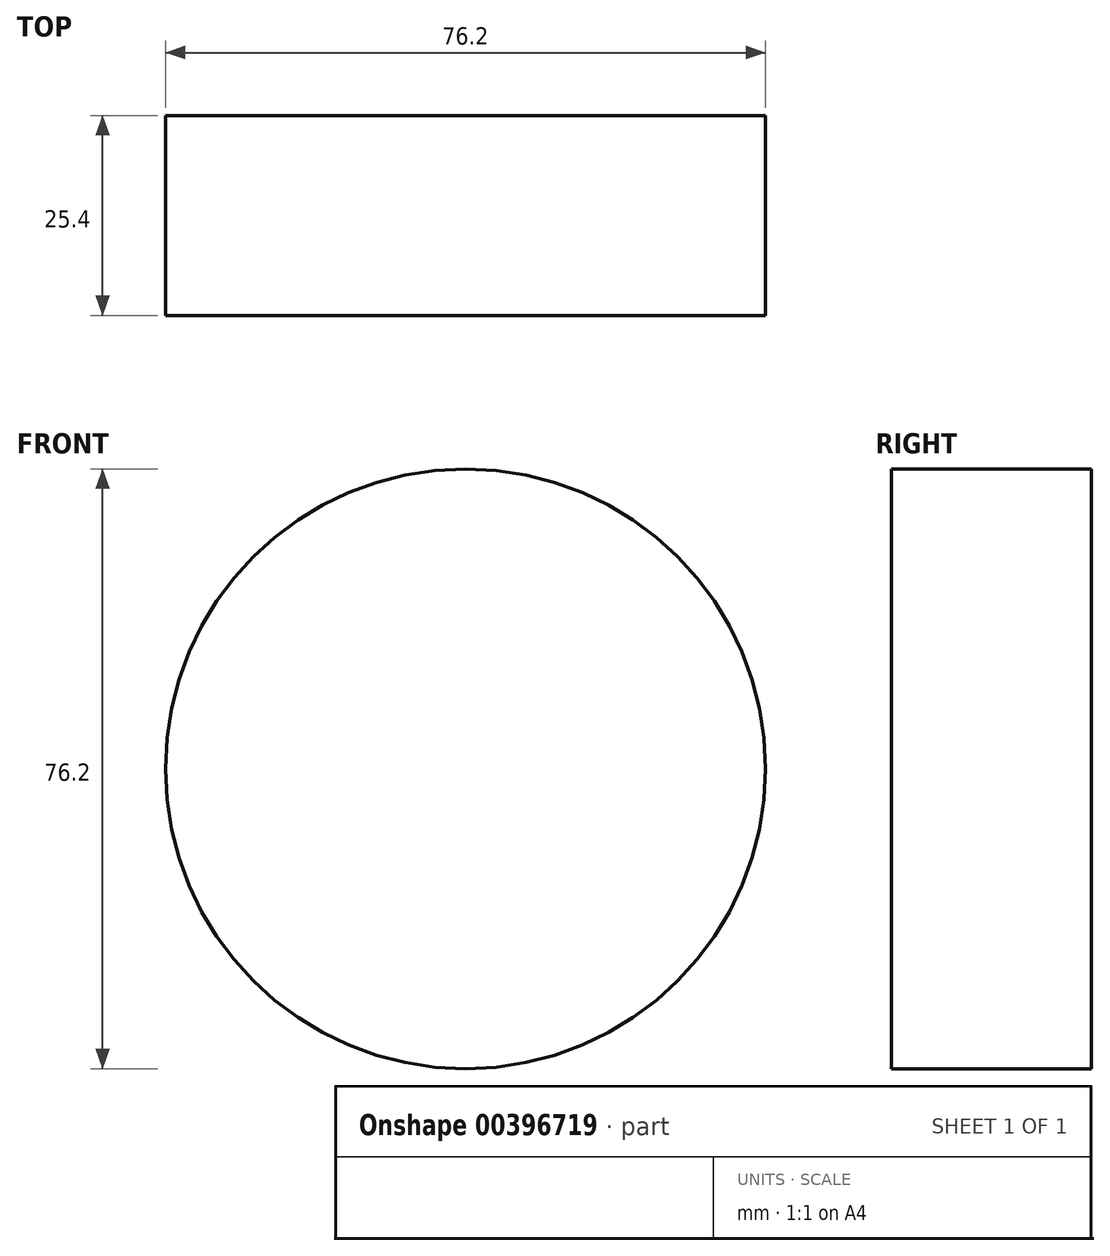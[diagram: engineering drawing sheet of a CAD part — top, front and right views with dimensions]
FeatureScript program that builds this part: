
annotation { "Feature Type Name" : "Feature", "Feature Type Description" : "" }
export const myFeature = defineFeature(function(context is Context, id is Id, definition is map)
    precondition{}
    {
        {
            var Q0;
            Q0=qCreatedBy(makeId("Front.planeOp"),FACE);
            var sketch = newSketch(context, id + "F0", { "sketchPlane" : qUnion([Q0])});
            skCircle(sketch, "E0", {"center": v(0, 0) * mm, "radius": 38.1 * mm});
            skSolve(sketch);
        }
        {
            var Q0;
            Q0=makeQuery(id+"F0.imprint","IMPRINT",FACE,{"disambiguationData":[TD([[makeQuery(id+"F0.imprint","IMPRINT",EDGE,{"derivedFrom":sQuery(id+"F0.wireOp",EDGE,"E0")}),1.0]])]});
            extrude(context, id + "F1", {"entities" : qUnion([Q0]), "depth" : 25.4 * mm});
        }
        {
            var Q0;
            Q0=qCreatedBy(makeId("Front.planeOp"),FACE);
            var sketch = newSketch(context, id + "F2", { "sketchPlane" : qUnion([Q0])});
            skCircle(sketch, "E1", {"center": v(-20.59, 20.1) * mm, "radius": 4.92 * mm});
            skCircle(sketch, "E2", {"center": v(0, 19.52) * mm, "radius": 4.68 * mm});
            skCircle(sketch, "E3", {"center": v(19.16, 19.52) * mm, "radius": 4.76 * mm});
            skSolve(sketch);
        }
        {
            var Q0;
            Q0=sQuery(id+"F2.wireOp",EDGE,"E1");
            var Q1;
            Q1=sQuery(id+"F2.wireOp",EDGE,"E2");
            var Q2;
            Q2=sQuery(id+"F2.wireOp",EDGE,"E3");
            extrude(context, id + "F3", {"bodyType" : ToolBodyType.SURFACE, "surfaceEntities" : qUnion([Q0, Q1, Q2]), "depth" : 101.6 * mm});
        }
    });
